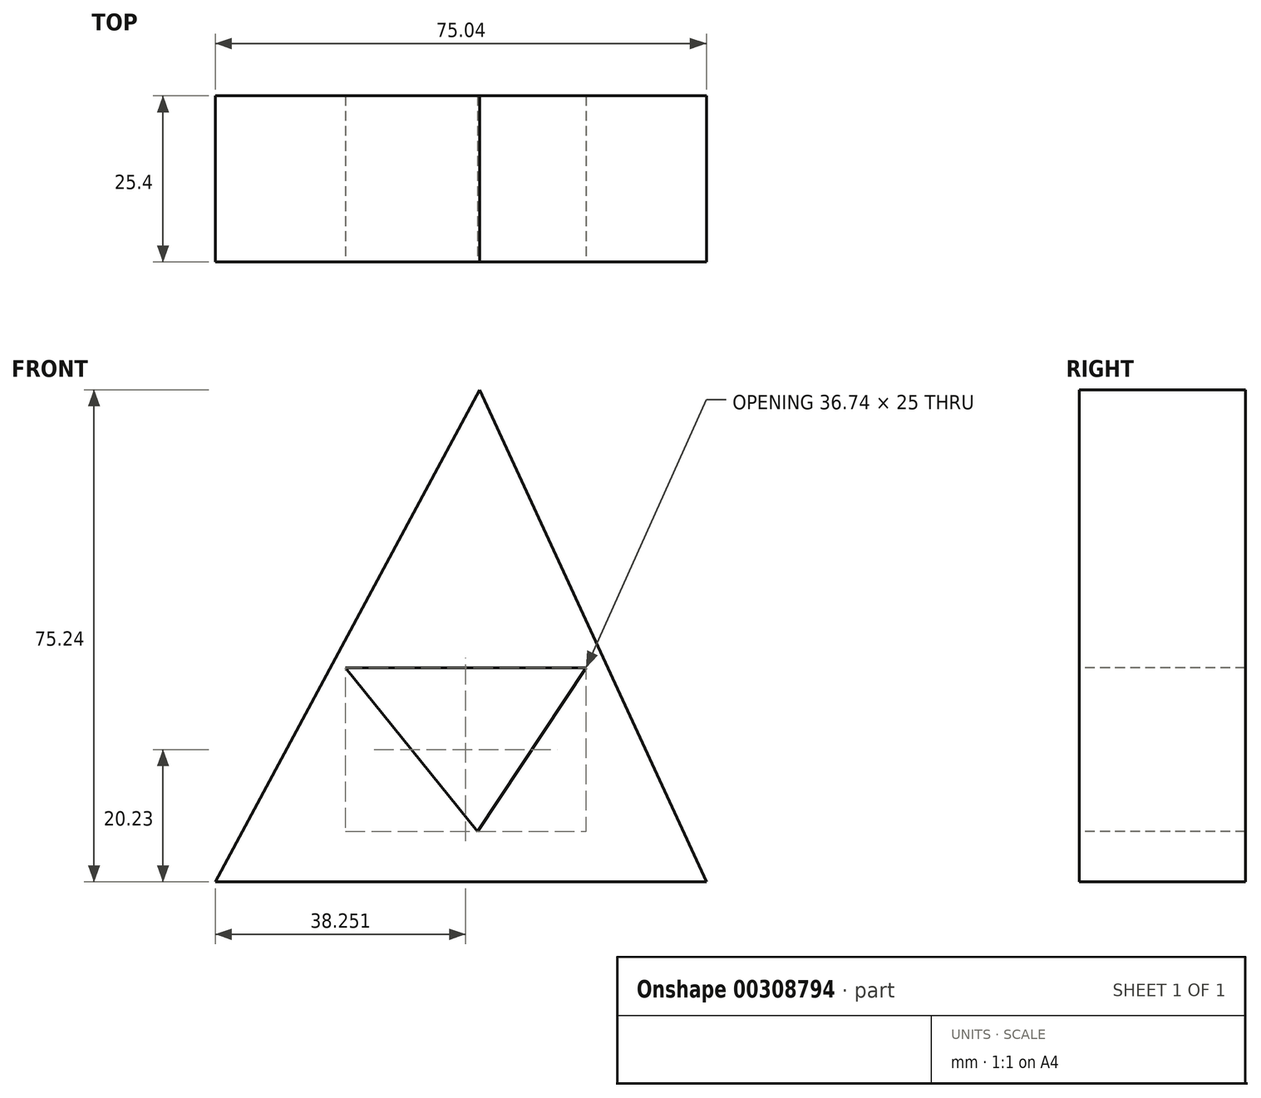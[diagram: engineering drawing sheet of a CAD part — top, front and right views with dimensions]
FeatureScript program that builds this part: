
annotation { "Feature Type Name" : "Feature", "Feature Type Description" : "" }
export const myFeature = defineFeature(function(context is Context, id is Id, definition is map)
    precondition{}
    {
        {
            var Q0;
            Q0=qCreatedBy(makeId("Front.planeOp"),FACE);
            var sketch = newSketch(context, id + "F0", { "sketchPlane" : qUnion([Q0])});
            skLineSegment(sketch, "E0", {"start": v(40.36, 75.24) * mm, "end": v(0, 0) * mm});
            skLineSegment(sketch, "E1", {"start": v(0, 0) * mm, "end": v(75.04, 0) * mm});
            skLineSegment(sketch, "E2", {"start": v(75.04, 0) * mm, "end": v(40.36, 75.24) * mm});
            skLineSegment(sketch, "E3", {"start": v(58.02, 36.92) * mm, "end": v(40.36, 0) * mm});
            skLineSegment(sketch, "E4", {"start": v(40.36, 0) * mm, "end": v(20, 37.3) * mm});
            skLineSegment(sketch, "E5", {"start": v(20, 37.3) * mm, "end": v(58.02, 36.92) * mm});
            skSolve(sketch);
        }
        {
            var Q0;
            Q0 = qSketchRegion(id + "F0", true);
            extrude(context, id + "F1", {"entities" : qUnion([Q0]), "depth" : 25.4 * mm});
        }
        {
            var Q0;
            Q0=qCreatedBy(makeId("Front.planeOp"),FACE);
            var sketch = newSketch(context, id + "F2", { "sketchPlane" : qUnion([Q0])});
            skLineSegment(sketch, "E6", {"start": v(19.88, 32.73) * mm, "end": v(56.62, 32.73) * mm});
            skLineSegment(sketch, "E7", {"start": v(56.62, 32.73) * mm, "end": v(40.06, 7.73) * mm});
            skLineSegment(sketch, "E8", {"start": v(40.06, 7.73) * mm, "end": v(19.88, 32.73) * mm});
            skSolve(sketch);
        }
        {
            var Q0;
            Q0 = qSketchRegion(id + "F2", true);
            extrude(context, id + "F3", {"entities" : qUnion([Q0]), "operationType" : NewBodyOperationType.REMOVE, "endBound" : BoundingType.SYMMETRIC, "oppositeDirection" : true, "depth" : 50.8 * mm});
        }
    });
